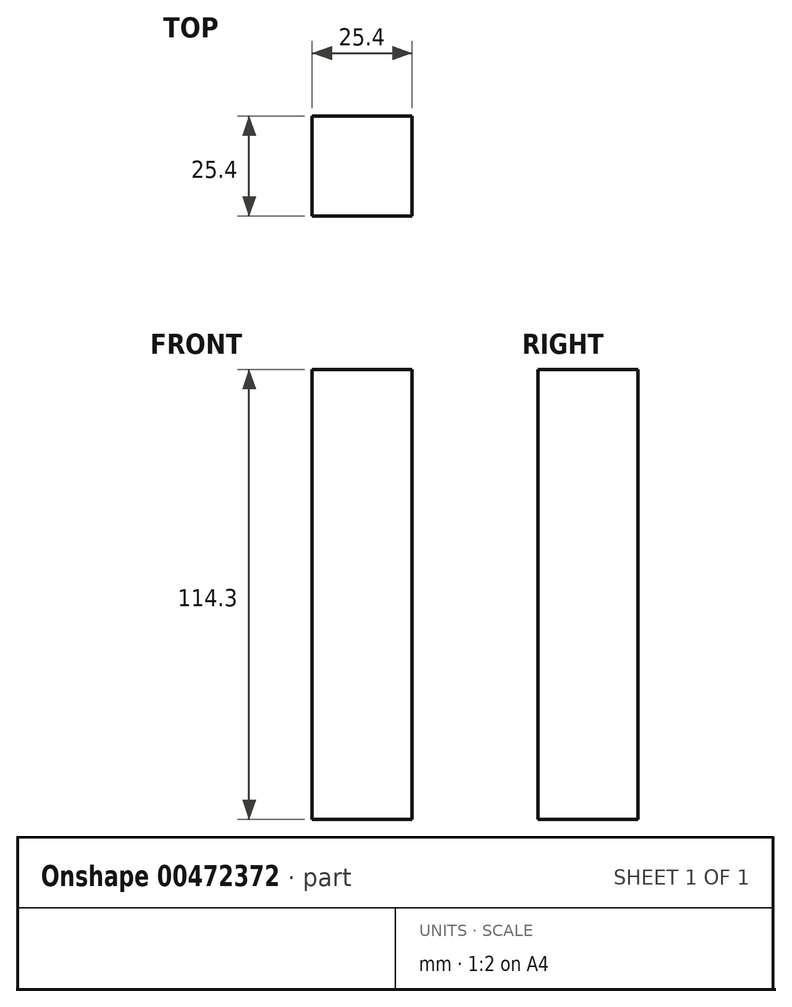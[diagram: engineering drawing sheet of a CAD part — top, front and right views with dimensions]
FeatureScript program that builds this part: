
annotation { "Feature Type Name" : "Feature", "Feature Type Description" : "" }
export const myFeature = defineFeature(function(context is Context, id is Id, definition is map)
    precondition{}
    {
        {
            var Q0;
            Q0=qCreatedBy(makeId("Front.planeOp"),FACE);
            var sketch = newSketch(context, id + "F0", { "sketchPlane" : qUnion([Q0])});
            skLineSegment(sketch, "E0.bottom", {"start": v(-36.47, -51.2) * mm, "end": v(-11.07, -51.2) * mm});
            skLineSegment(sketch, "E0.top", {"start": v(-36.47, 63.1) * mm, "end": v(-11.07, 63.1) * mm});
            skLineSegment(sketch, "E0.left", {"start": v(-36.47, -51.2) * mm, "end": v(-36.47, 63.1) * mm});
            skLineSegment(sketch, "E0.right", {"start": v(-11.07, -51.2) * mm, "end": v(-11.07, 63.1) * mm});
            skSolve(sketch);
        }
        {
            var Q0;
            Q0=makeQuery(id+"F0.imprint","IMPRINT",FACE,{"disambiguationData":[TD([[makeQuery(id+"F0.imprint","IMPRINT",EDGE,{"derivedFrom":sQuery(id+"F0.wireOp",EDGE,"E0.bottom")}),1.0]])]});
            extrude(context, id + "F1", {"entities" : qUnion([Q0]), "depth" : 25.4 * mm});
        }
    });
